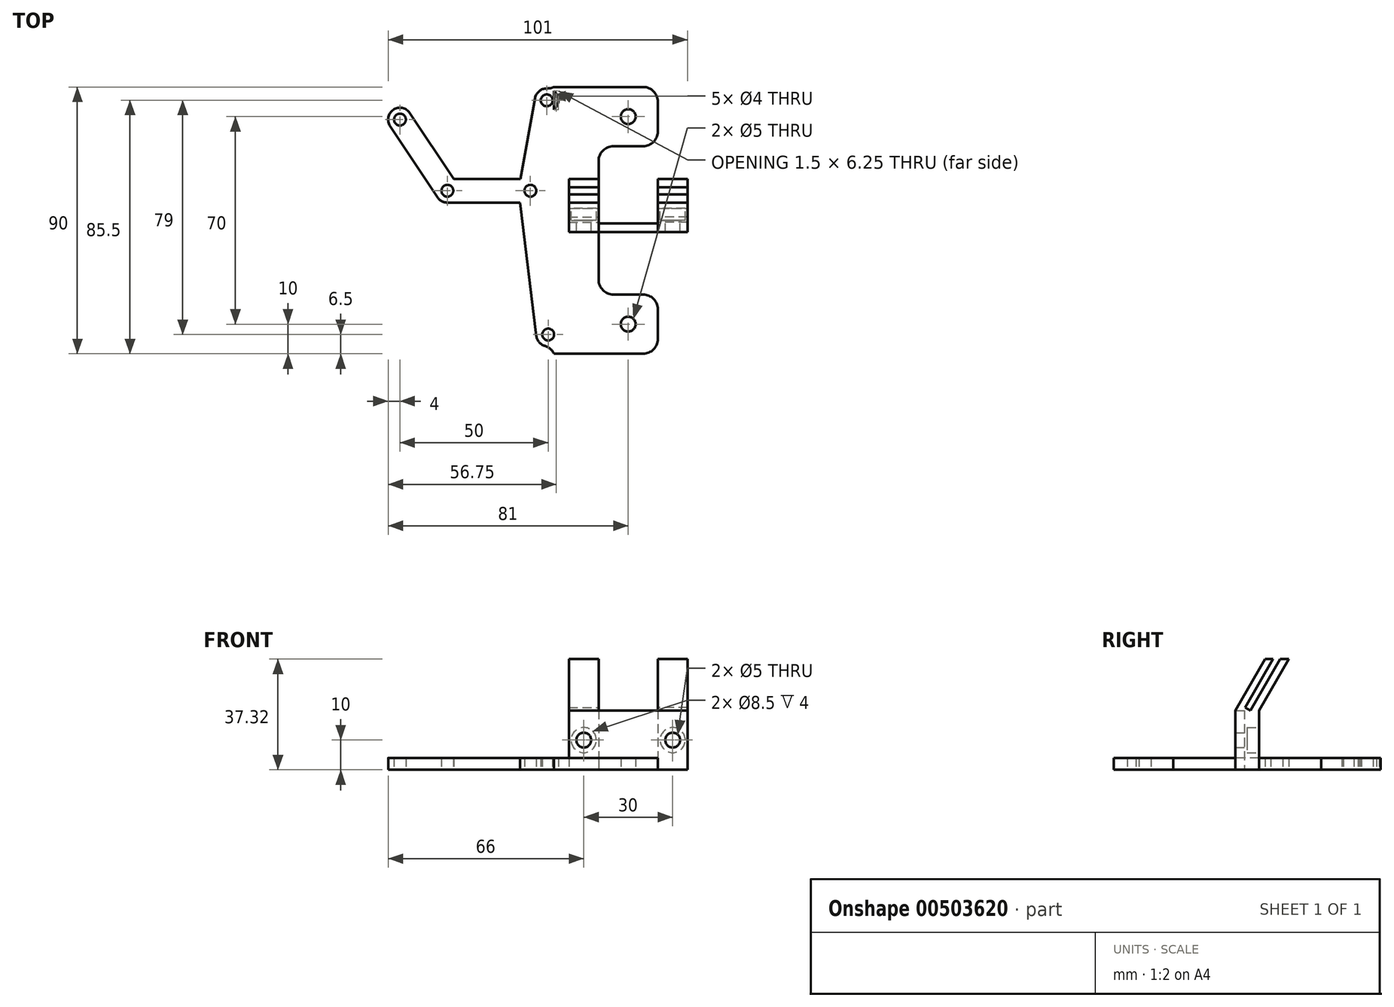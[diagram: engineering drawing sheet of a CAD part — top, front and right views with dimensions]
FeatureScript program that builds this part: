
annotation { "Feature Type Name" : "Feature", "Feature Type Description" : "" }
export const myFeature = defineFeature(function(context is Context, id is Id, definition is map)
    precondition{}
    {
        {
            var Q0;
            Q0=qCreatedBy(makeId("Top.planeOp"),FACE);
            var sketch = newSketch(context, id + "F0", { "sketchPlane" : qUnion([Q0])});
            skLineSegment(sketch, "E0.bottom", {"start": v(-20, 4) * mm, "end": v(20, 4) * mm});
            skLineSegment(sketch, "E0.top", {"start": v(-20, -4) * mm, "end": v(20, -4) * mm});
            skLineSegment(sketch, "E0.left", {"start": v(-20, 4) * mm, "end": v(-20, -4) * mm});
            skLineSegment(sketch, "E0.right", {"start": v(20, 4) * mm, "end": v(20, -4) * mm});
            skPoint(sketch, "E0.middle", {"position": v(0, 0) * mm});
            skLineSegment(sketch, "E1", {"start": v(-10, 4) * mm, "end": v(-10, -4) * mm});
            skLineSegment(sketch, "E2", {"start": v(10, 4) * mm, "end": v(10, -4) * mm});
            skLineSegment(sketch, "E3", {"start": v(-10, 0) * mm, "end": v(10, 0) * mm});
            skSolve(sketch);
        }
        {
            var Q0;
            {var subQ5=sQuery(id+"F0.wireOp",EDGE,"E3");Q0=makeQuery(id+"F0.imprint","IMPRINT",FACE,{"disambiguationData":[TD([[makeQuery(id+"F0.imprint","IMPRINT",EDGE,{"derivedFrom":subQ5}),-1.0]])]});}
            extrude(context, id + "F1", {"entities" : qUnion([Q0]), "depth" : 20 * mm, "offsetDistance" : 25 * mm});
        }
        {
            var Q0;
            {var subQ0=sQuery(id+"F0.wireOp",EDGE,"E0.left");Q0=makeQuery(id+"F0.imprint","IMPRINT",FACE,{"disambiguationData":[TD([[makeQuery(id+"F0.imprint","IMPRINT",EDGE,{"derivedFrom":subQ0}),1.0]])]});}
            var Q1;
            {var subQ4=sQuery(id+"F0.wireOp",EDGE,"E0.right");Q1=makeQuery(id+"F0.imprint","IMPRINT",FACE,{"disambiguationData":[TD([[makeQuery(id+"F0.imprint","IMPRINT",EDGE,{"derivedFrom":subQ4}),-1.0]])]});}
            extrude(context, id + "F2", {"entities" : qUnion([Q0, Q1]), "operationType" : NewBodyOperationType.ADD, "depth" : 20 * mm, "offsetDistance" : 25 * mm});
        }
        {
            var Q0;
            Q0=qCreatedBy(makeId("Right.planeOp"),FACE);
            var sketch = newSketch(context, id + "F3", { "sketchPlane" : qUnion([Q0])});
            skLineSegment(sketch, "E4.0", {"start": v(4, 20) * mm, "end": v(-4, 20) * mm});
            skLineSegment(sketch, "E5", {"start": v(-4, 20) * mm, "end": v(6, 37.32) * mm});
            skLineSegment(sketch, "E6", {"start": v(4, 20) * mm, "end": v(14, 37.32) * mm});
            skLineSegment(sketch, "E7", {"start": v(6, 37.32) * mm, "end": v(14, 37.32) * mm});
            skLineSegment(sketch, "E8", {"start": v(8.77, 37.32) * mm, "end": v(-1.23, 20) * mm});
            skLineSegment(sketch, "E9", {"start": v(11.14, 37.32) * mm, "end": v(1.14, 20) * mm});
            skLineSegment(sketch, "E10", {"start": v(1.14, 20) * mm, "end": v(-0.64, 21.02) * mm});
            skSolve(sketch);
        }
        {
            var Q0;
            {var subQ1=sQuery(id+"F3.wireOp",EDGE,"E5");Q0=makeQuery(id+"F3.imprint","IMPRINT",FACE,{"disambiguationData":[TD([[makeQuery(id+"F3.imprint","IMPRINT",EDGE,{"derivedFrom":subQ1}),-1.0]])]});}
            var Q1;
            {var subQ3=sQuery(id+"F3.wireOp",EDGE,"E10");Q1=makeQuery(id+"F3.imprint","IMPRINT",FACE,{"disambiguationData":[TD([[makeQuery(id+"F3.imprint","IMPRINT",EDGE,{"derivedFrom":subQ3}),1.0]])]});}
            var Q2;
            {var subQ0=sQuery(id+"F3.wireOp",EDGE,"E6");Q2=makeQuery(id+"F3.imprint","IMPRINT",FACE,{"disambiguationData":[TD([[makeQuery(id+"F3.imprint","IMPRINT",EDGE,{"derivedFrom":subQ0}),1.0]])]});}
            var Q3;
            Q3=makeQuery(id+"F2.opExtrude","SWEPT_FACE",FACE,{"disambiguationData":[OSD([sQuery(id+"F0.wireOp",EDGE,"E0.right")])]});
            var Q4;
            Q4=makeQuery(id+"F2.opExtrude","SWEPT_FACE",FACE,{"disambiguationData":[OSD([sQuery(id+"F0.wireOp",EDGE,"E2")])]});
            extrude(context, id + "F4", {"entities" : qUnion([Q0, Q1, Q2]), "operationType" : NewBodyOperationType.ADD, "endBound" : BoundingType.UP_TO_SURFACE, "depth" : 25 * mm, "endBoundEntityFace" : qUnion([Q3]), "offsetDistance" : 25 * mm, "hasSecondDirection" : true, "secondDirectionBound" : SecondDirectionBoundingType.UP_TO_SURFACE, "secondDirectionOppositeDirection" : false, "secondDirectionDepth" : 14.1 * mm, "secondDirectionBoundEntityFace" : qUnion([Q4])});
        }
        {
            var Q0;
            {var subQ0=sQuery(id+"F3.wireOp",EDGE,"E6");Q0=makeQuery(id+"F3.imprint","IMPRINT",FACE,{"disambiguationData":[TD([[makeQuery(id+"F3.imprint","IMPRINT",EDGE,{"derivedFrom":subQ0}),1.0]])]});}
            var Q1;
            {var subQ1=sQuery(id+"F3.wireOp",EDGE,"E5");Q1=makeQuery(id+"F3.imprint","IMPRINT",FACE,{"disambiguationData":[TD([[makeQuery(id+"F3.imprint","IMPRINT",EDGE,{"derivedFrom":subQ1}),-1.0]])]});}
            var Q2;
            {var subQ3=sQuery(id+"F3.wireOp",EDGE,"E10");Q2=makeQuery(id+"F3.imprint","IMPRINT",FACE,{"disambiguationData":[TD([[makeQuery(id+"F3.imprint","IMPRINT",EDGE,{"derivedFrom":subQ3}),1.0]])]});}
            var Q3;
            Q3=makeQuery(id+"F2.opExtrude","SWEPT_FACE",FACE,{"disambiguationData":[OSD([sQuery(id+"F0.wireOp",EDGE,"E0.left")])]});
            var Q4;
            Q4=makeQuery(id+"F2.opExtrude","SWEPT_FACE",FACE,{"disambiguationData":[OSD([sQuery(id+"F0.wireOp",EDGE,"E1")])]});
            extrude(context, id + "F5", {"entities" : qUnion([Q0, Q1, Q2]), "operationType" : NewBodyOperationType.ADD, "endBound" : BoundingType.UP_TO_SURFACE, "oppositeDirection" : true, "depth" : 25 * mm, "endBoundEntityFace" : qUnion([Q3]), "offsetDistance" : 25 * mm, "hasSecondDirection" : true, "secondDirectionBound" : SecondDirectionBoundingType.UP_TO_SURFACE, "secondDirectionOppositeDirection" : true, "secondDirectionDepth" : 25 * mm, "secondDirectionBoundEntityFace" : qUnion([Q4])});
        }
        {
            var Q0;
            {var subQ0=sQuery(id+"F0.wireOp",EDGE,"E0.bottom");Q0=makeQuery(id+"F2.opExtrude","SWEPT_FACE",FACE,{"disambiguationData":[OSD([subQ0]),TDD([makeQuery(id+"F0.imprint","IMPRINT",EDGE,{"disambiguationData":[TD([[makeQuery(id+"F0.imprint","INTERSECT",VERTEX,{"derivedFrom":[subQ0,sQuery(id+"F0.wireOp",EDGE,"E0.right")]}),1.0]])],"derivedFrom":subQ0})])]});}
            var sketch = newSketch(context, id + "F6", { "sketchPlane" : qUnion([Q0])});
            skLineSegment(sketch, "E11.0.0", {"start": v(10, 0) * mm, "end": v(20, 0) * mm});
            skLineSegment(sketch, "E11.0.1", {"start": v(20, 0) * mm, "end": v(20, 20) * mm});
            skLineSegment(sketch, "E11.0.2", {"start": v(20, 20) * mm, "end": v(10, 20) * mm});
            skLineSegment(sketch, "E11.0.3", {"start": v(10, 20) * mm, "end": v(10, 0) * mm});
            skCircle(sketch, "E12", {"center": v(-15, 10) * mm, "radius": 4.25 * mm});
            skPoint(sketch, "E12.centerSnap0", {"position": v(-15, 20) * mm});
            skPoint(sketch, "E12.centerSnap1", {"position": v(-20, 10) * mm});
            skCircle(sketch, "E13", {"center": v(15, 10) * mm, "radius": 4.25 * mm});
            skPoint(sketch, "E13.centerSnap0", {"position": v(10, 10) * mm});
            skPoint(sketch, "E13.centerSnap1", {"position": v(15, 20) * mm});
            skCircle(sketch, "E14", {"center": v(-15, 10) * mm, "radius": 2.5 * mm});
            skCircle(sketch, "E15", {"center": v(15, 10) * mm, "radius": 2.5 * mm});
            skSolve(sketch);
        }
        {
            var Q0;
            Q0=makeQuery(id+"F6.imprint","IMPRINT",FACE,{"disambiguationData":[TD([[makeQuery(id+"F6.imprint","IMPRINT",EDGE,{"derivedFrom":sQuery(id+"F6.wireOp",EDGE,"E14")}),1.0]])]});
            var Q1;
            Q1=makeQuery(id+"F6.imprint","IMPRINT",FACE,{"disambiguationData":[TD([[makeQuery(id+"F6.imprint","IMPRINT",EDGE,{"derivedFrom":sQuery(id+"F6.wireOp",EDGE,"E15")}),1.0]])]});
            extrude(context, id + "F7", {"entities" : qUnion([Q0, Q1]), "operationType" : NewBodyOperationType.REMOVE, "oppositeDirection" : true, "depth" : 25 * mm, "offsetDistance" : 25 * mm});
        }
        {
            var Q0;
            Q0=makeQuery(id+"F6.imprint","IMPRINT",FACE,{"disambiguationData":[TD([[makeQuery(id+"F6.imprint","IMPRINT",EDGE,{"derivedFrom":sQuery(id+"F6.wireOp",EDGE,"E12")}),1.0]])]});
            var Q1;
            Q1=makeQuery(id+"F6.imprint","IMPRINT",FACE,{"disambiguationData":[TD([[makeQuery(id+"F6.imprint","IMPRINT",EDGE,{"derivedFrom":sQuery(id+"F6.wireOp",EDGE,"E13")}),1.0]])]});
            extrude(context, id + "F8", {"entities" : qUnion([Q0, Q1]), "operationType" : NewBodyOperationType.REMOVE, "oppositeDirection" : true, "depth" : 4 * mm, "offsetDistance" : 25 * mm});
        }
        {
            var Q0;
            Q0=makeQuery(id+"F1.opExtrude","SWEPT_FACE",FACE,{"disambiguationData":[OSD([sQuery(id+"F0.wireOp",EDGE,"E3")])]});
            extrude(context, id + "F9", {"entities" : qUnion([Q0]), "operationType" : NewBodyOperationType.REMOVE, "oppositeDirection" : true, "depth" : 1 * mm, "offsetDistance" : 25 * mm});
        }
        {
            var Q0;
            Q0=qCreatedBy(makeId("Top.planeOp"),FACE);
            var sketch = newSketch(context, id + "F10", { "sketchPlane" : qUnion([Q0])});
            skLineSegment(sketch, "E16.bottom", {"start": v(-10, 45) * mm, "end": v(10, 45) * mm});
            skLineSegment(sketch, "E16.top", {"start": v(-10, -45) * mm, "end": v(10, -45) * mm});
            skLineSegment(sketch, "E16.left", {"start": v(-10, 45) * mm, "end": v(-10, -45) * mm});
            skLineSegment(sketch, "E16.right", {"start": v(10, 45) * mm, "end": v(10, -45) * mm});
            skPoint(sketch, "E16.middle", {"position": v(0, 0) * mm});
            skLineSegment(sketch, "E17.bottom", {"start": v(-10, 45) * mm, "end": v(-25, 45) * mm});
            skLineSegment(sketch, "E17.top", {"start": v(-10, -45) * mm, "end": v(-25, -45) * mm});
            skLineSegment(sketch, "E17.right", {"start": v(-25, 45) * mm, "end": v(-25, -45) * mm});
            skPoint(sketch, "E18", {"position": v(-27.5, 40.5) * mm});
            skCircle(sketch, "E19", {"center": v(-27.5, 40.5) * mm, "radius": 2 * mm});
            skPoint(sketch, "E20", {"position": v(-27, -38.5) * mm});
            skCircle(sketch, "E21", {"center": v(-27, -38.5) * mm, "radius": 2 * mm});
            skPoint(sketch, "E22", {"position": v(-33, 10) * mm});
            skPoint(sketch, "E23", {"position": v(-61, 10) * mm});
            skPoint(sketch, "E24", {"position": v(-77, 34) * mm});
            skCircle(sketch, "E25", {"center": v(-77, 34) * mm, "radius": 2 * mm});
            skCircle(sketch, "E26", {"center": v(-61, 10) * mm, "radius": 2 * mm});
            skCircle(sketch, "E27", {"center": v(-33, 10) * mm, "radius": 2 * mm});
            skCircle(sketch, "E28", {"center": v(-77, 34) * mm, "radius": 4 * mm});
            skCircle(sketch, "E29", {"center": v(-61, 10) * mm, "radius": 4 * mm});
            skCircle(sketch, "E30", {"center": v(-33, 10) * mm, "radius": 4 * mm});
            skCircle(sketch, "E31", {"center": v(-27.5, 40.5) * mm, "radius": 4 * mm});
            skCircle(sketch, "E32", {"center": v(-27, -38.5) * mm, "radius": 4 * mm});
            skLineSegment(sketch, "E33", {"start": v(-77, 34) * mm, "end": v(-61, 10) * mm, "construction": true});
            skLineSegment(sketch, "E34", {"start": v(-61, 10) * mm, "end": v(-33, 10) * mm, "construction": true});
            skLineSegment(sketch, "E35", {"start": v(-33, 10) * mm, "end": v(-27.5, 40.5) * mm, "construction": true});
            skLineSegment(sketch, "E36", {"start": v(-33, 10) * mm, "end": v(-27, -38.5) * mm, "construction": true});
            skLineSegment(sketch, "E37", {"start": v(-33, 14) * mm, "end": v(-25, 14) * mm});
            skLineSegment(sketch, "E38", {"start": v(-33, 6) * mm, "end": v(-25, 6) * mm});
            skLineSegment(sketch, "E39", {"start": v(-27.5, 44.5) * mm, "end": v(-25, 44.5) * mm});
            skLineSegment(sketch, "E40", {"start": v(-27.5, 36.5) * mm, "end": v(-25, 36.5) * mm});
            skLineSegment(sketch, "E41", {"start": v(-27, -34.5) * mm, "end": v(-25, -34.5) * mm});
            skLineSegment(sketch, "E42", {"start": v(-27, -42.5) * mm, "end": v(-25, -42.5) * mm});
            skLineSegment(sketch, "E43.0", {"start": v(-36.97, 9.5) * mm, "end": v(-30.97, -39) * mm});
            skLineSegment(sketch, "E44.0", {"start": v(-29.03, 10.5) * mm, "end": v(-23.03, -38) * mm});
            skLineSegment(sketch, "E45.0", {"start": v(-29.06, 9.3) * mm, "end": v(-23.56, 39.8) * mm});
            skLineSegment(sketch, "E46.0", {"start": v(-36.94, 10.7) * mm, "end": v(-31.44, 41.2) * mm});
            skLineSegment(sketch, "E47.0", {"start": v(-80.33, 31.78) * mm, "end": v(-64.33, 7.78) * mm});
            skLineSegment(sketch, "E48.0", {"start": v(-73.67, 36.22) * mm, "end": v(-57.67, 12.22) * mm});
            skLineSegment(sketch, "E49.0", {"start": v(-61, 6) * mm, "end": v(-33, 6) * mm});
            skLineSegment(sketch, "E50.0", {"start": v(-61, 14) * mm, "end": v(-33, 14) * mm});
            skCircle(sketch, "E51", {"center": v(0, 35) * mm, "radius": 2.5 * mm});
            skPoint(sketch, "E51.centerSnap0", {"position": v(0, 45) * mm});
            skCircle(sketch, "E52", {"center": v(0, -35) * mm, "radius": 2.5 * mm});
            skPoint(sketch, "E52.centerSnap0", {"position": v(0, -45) * mm});
            skLineSegment(sketch, "E53.bottom", {"start": v(-10, 25) * mm, "end": v(10, 25) * mm});
            skLineSegment(sketch, "E53.top", {"start": v(-10, -25) * mm, "end": v(10, -25) * mm});
            skLineSegment(sketch, "E53.left", {"start": v(-10, 25) * mm, "end": v(-10, -25) * mm});
            skLineSegment(sketch, "E53.right", {"start": v(10, 25) * mm, "end": v(10, -25) * mm});
            skSolve(sketch);
        }
        {
            var Q0;
            {var subQ1=sQuery(id+"F10.wireOp",EDGE,"E16.bottom");Q0=makeQuery(id+"F10.imprint","IMPRINT",FACE,{"disambiguationData":[TD([[makeQuery(id+"F10.imprint","IMPRINT",EDGE,{"derivedFrom":subQ1}),-1.0]])]});}
            var Q1;
            {var subQ12=sQuery(id+"F10.wireOp",EDGE,"E17.bottom");Q1=makeQuery(id+"F10.imprint","IMPRINT",FACE,{"disambiguationData":[TD([[makeQuery(id+"F10.imprint","IMPRINT",EDGE,{"derivedFrom":subQ12}),1.0]])]});}
            var Q2;
            {var subQ1=sQuery(id+"F10.wireOp",EDGE,"E16.top");Q2=makeQuery(id+"F10.imprint","IMPRINT",FACE,{"disambiguationData":[TD([[makeQuery(id+"F10.imprint","IMPRINT",EDGE,{"derivedFrom":subQ1}),1.0]])]});}
            var Q3;
            {var subQ7=sQuery(id+"F10.wireOp",EDGE,"E41");Q3=makeQuery(id+"F10.imprint","IMPRINT",FACE,{"disambiguationData":[TD([[makeQuery(id+"F10.imprint","IMPRINT",EDGE,{"derivedFrom":subQ7}),1.0]])]});}
            var Q4;
            {var subQ5=sQuery(id+"F10.wireOp",EDGE,"E37");var subQ6=sQuery(id+"F10.wireOp",EDGE,"E17.right");var subQ7=makeQuery(id+"F10.imprint","INTERSECT",VERTEX,{"derivedFrom":[subQ6,subQ5]});Q4=makeQuery(id+"F10.imprint","IMPRINT",FACE,{"disambiguationData":[TD([[makeQuery(id+"F10.imprint","IMPRINT",EDGE,{"disambiguationData":[TD([[subQ7,-1.0]])],"derivedFrom":subQ6}),-1.0]])]});}
            var Q5;
            {var subQ0=sQuery(id+"F10.wireOp",EDGE,"E17.right");var subQ1=makeQuery(id+"F10.imprint","INTERSECT",VERTEX,{"derivedFrom":[subQ0,sQuery(id+"F10.wireOp",EDGE,"E41")]});Q5=makeQuery(id+"F10.imprint","IMPRINT",FACE,{"disambiguationData":[TD([[makeQuery(id+"F10.imprint","IMPRINT",EDGE,{"disambiguationData":[TD([[subQ1,1.0]])],"derivedFrom":subQ0}),1.0]])]});}
            var Q6;
            {var subQ0=sQuery(id+"F10.wireOp",EDGE,"E41");Q6=makeQuery(id+"F10.imprint","IMPRINT",FACE,{"disambiguationData":[TD([[makeQuery(id+"F10.imprint","IMPRINT",EDGE,{"derivedFrom":subQ0}),-1.0]])]});}
            var Q7;
            {var subQ0=sQuery(id+"F10.wireOp",EDGE,"E17.right");var subQ1=makeQuery(id+"F10.imprint","INTERSECT",VERTEX,{"derivedFrom":[subQ0,sQuery(id+"F10.wireOp",EDGE,"E21")]});Q7=makeQuery(id+"F10.imprint","IMPRINT",FACE,{"disambiguationData":[TD([[makeQuery(id+"F10.imprint","IMPRINT",EDGE,{"disambiguationData":[TD([[subQ1,1.0]])],"derivedFrom":subQ0}),1.0]])]});}
            var Q8;
            {var subQ4=sQuery(id+"F10.wireOp",EDGE,"E21");Q8=makeQuery(id+"F10.imprint","IMPRINT",FACE,{"disambiguationData":[TD([[makeQuery(id+"F10.imprint","IMPRINT",EDGE,{"derivedFrom":subQ4}),-1.0]])]});}
            var Q9;
            {var subQ0=sQuery(id+"F10.wireOp",EDGE,"E42");Q9=makeQuery(id+"F10.imprint","IMPRINT",FACE,{"disambiguationData":[TD([[makeQuery(id+"F10.imprint","IMPRINT",EDGE,{"derivedFrom":subQ0}),1.0]])]});}
            var Q10;
            {var subQ0=sQuery(id+"F10.wireOp",EDGE,"E38");var subQ1=sQuery(id+"F10.wireOp",EDGE,"E17.right");var subQ2=makeQuery(id+"F10.imprint","INTERSECT",VERTEX,{"derivedFrom":[subQ1,subQ0]});Q10=makeQuery(id+"F10.imprint","IMPRINT",FACE,{"disambiguationData":[TD([[makeQuery(id+"F10.imprint","IMPRINT",EDGE,{"disambiguationData":[TD([[subQ2,-1.0]])],"derivedFrom":subQ1}),-1.0]])]});}
            var Q11;
            {var subQ0=sQuery(id+"F10.wireOp",EDGE,"E37");var subQ1=sQuery(id+"F10.wireOp",EDGE,"E17.right");var subQ2=makeQuery(id+"F10.imprint","INTERSECT",VERTEX,{"derivedFrom":[subQ1,subQ0]});Q11=makeQuery(id+"F10.imprint","IMPRINT",FACE,{"disambiguationData":[TD([[makeQuery(id+"F10.imprint","IMPRINT",EDGE,{"disambiguationData":[TD([[subQ2,1.0]])],"derivedFrom":subQ1}),-1.0]])]});}
            var Q12;
            {var subQ0=sQuery(id+"F10.wireOp",EDGE,"E38");var subQ5=sQuery(id+"F10.wireOp",EDGE,"E44.0");var subQ6=makeQuery(id+"F10.imprint","INTERSECT",VERTEX,{"derivedFrom":[subQ0,subQ5]});Q12=makeQuery(id+"F10.imprint","IMPRINT",FACE,{"disambiguationData":[TD([[makeQuery(id+"F10.imprint","IMPRINT",EDGE,{"disambiguationData":[TD([[subQ6,1.0]])],"derivedFrom":subQ5}),-1.0]])]});}
            var Q13;
            {var subQ1=sQuery(id+"F10.wireOp",EDGE,"E30");var subQ3=sQuery(id+"F10.wireOp",EDGE,"E43.0");var subQ4=makeQuery(id+"F10.imprint","INTERSECT",VERTEX,{"derivedFrom":[subQ1,subQ3]});Q13=makeQuery(id+"F10.imprint","IMPRINT",FACE,{"disambiguationData":[TD([[makeQuery(id+"F10.imprint","IMPRINT",EDGE,{"disambiguationData":[TD([[subQ4,-1.0]])],"derivedFrom":subQ3}),1.0]])]});}
            var Q14;
            {var subQ1=sQuery(id+"F10.wireOp",EDGE,"E30");var subQ3=sQuery(id+"F10.wireOp",EDGE,"E46.0");var subQ4=makeQuery(id+"F10.imprint","INTERSECT",VERTEX,{"derivedFrom":[subQ1,subQ3]});Q14=makeQuery(id+"F10.imprint","IMPRINT",FACE,{"disambiguationData":[TD([[makeQuery(id+"F10.imprint","IMPRINT",EDGE,{"disambiguationData":[TD([[subQ4,-1.0]])],"derivedFrom":subQ3}),-1.0]])]});}
            var Q15;
            {var subQ1=sQuery(id+"F10.wireOp",EDGE,"E30");var subQ3=sQuery(id+"F10.wireOp",EDGE,"E44.0");var subQ4=makeQuery(id+"F10.imprint","INTERSECT",VERTEX,{"derivedFrom":[subQ1,subQ3]});Q15=makeQuery(id+"F10.imprint","IMPRINT",FACE,{"disambiguationData":[TD([[makeQuery(id+"F10.imprint","IMPRINT",EDGE,{"disambiguationData":[TD([[subQ4,-1.0]])],"derivedFrom":subQ3}),1.0]])]});}
            var Q16;
            {var subQ0=sQuery(id+"F10.wireOp",EDGE,"E40");Q16=makeQuery(id+"F10.imprint","IMPRINT",FACE,{"disambiguationData":[TD([[makeQuery(id+"F10.imprint","IMPRINT",EDGE,{"derivedFrom":subQ0}),-1.0]])]});}
            var Q17;
            {var subQ0=sQuery(id+"F10.wireOp",EDGE,"E17.right");var subQ1=makeQuery(id+"F10.imprint","INTERSECT",VERTEX,{"derivedFrom":[subQ0,sQuery(id+"F10.wireOp",EDGE,"E40")]});Q17=makeQuery(id+"F10.imprint","IMPRINT",FACE,{"disambiguationData":[TD([[makeQuery(id+"F10.imprint","IMPRINT",EDGE,{"disambiguationData":[TD([[subQ1,1.0]])],"derivedFrom":subQ0}),1.0]])]});}
            var Q18;
            {var subQ0=sQuery(id+"F10.wireOp",EDGE,"E40");Q18=makeQuery(id+"F10.imprint","IMPRINT",FACE,{"disambiguationData":[TD([[makeQuery(id+"F10.imprint","IMPRINT",EDGE,{"derivedFrom":subQ0}),1.0]])]});}
            var Q19;
            Q19=makeQuery(id+"F10.imprint","IMPRINT",FACE,{"disambiguationData":[TD([[makeQuery(id+"F10.imprint","IMPRINT",EDGE,{"derivedFrom":sQuery(id+"F10.wireOp",EDGE,"E19")}),-1.0]])]});
            var Q20;
            {var subQ0=sQuery(id+"F10.wireOp",EDGE,"E31");var subQ1=sQuery(id+"F10.wireOp",EDGE,"E17.right");var subQ2=makeQuery(id+"F10.imprint","INTERSECT",VERTEX,{"disambiguationData":[OD(0.0)],"derivedFrom":[subQ1,subQ0]});Q20=makeQuery(id+"F10.imprint","IMPRINT",FACE,{"disambiguationData":[TD([[makeQuery(id+"F10.imprint","IMPRINT",EDGE,{"disambiguationData":[TD([[subQ2,-1.0]])],"derivedFrom":subQ1}),1.0]])]});}
            var Q21;
            {var subQ0=sQuery(id+"F10.wireOp",EDGE,"E39");Q21=makeQuery(id+"F10.imprint","IMPRINT",FACE,{"disambiguationData":[TD([[makeQuery(id+"F10.imprint","IMPRINT",EDGE,{"derivedFrom":subQ0}),-1.0]])]});}
            var Q22;
            {var subQ9=sQuery(id+"F10.wireOp",EDGE,"E48.0");var subQ10=sQuery(id+"F10.wireOp",EDGE,"E29");var subQ11=makeQuery(id+"F10.imprint","INTERSECT",VERTEX,{"derivedFrom":[subQ10,subQ9]});Q22=makeQuery(id+"F10.imprint","IMPRINT",FACE,{"disambiguationData":[TD([[makeQuery(id+"F10.imprint","IMPRINT",EDGE,{"disambiguationData":[TD([[subQ11,1.0]])],"derivedFrom":subQ10}),-1.0]])]});}
            var Q23;
            Q23=makeQuery(id+"F10.imprint","IMPRINT",FACE,{"disambiguationData":[TD([[makeQuery(id+"F10.imprint","IMPRINT",EDGE,{"derivedFrom":sQuery(id+"F10.wireOp",EDGE,"E26")}),-1.0]])]});
            var Q24;
            {var subQ0=sQuery(id+"F10.wireOp",EDGE,"E48.0");var subQ1=sQuery(id+"F10.wireOp",EDGE,"E29");var subQ2=makeQuery(id+"F10.imprint","INTERSECT",VERTEX,{"derivedFrom":[subQ1,subQ0]});Q24=makeQuery(id+"F10.imprint","IMPRINT",FACE,{"disambiguationData":[TD([[makeQuery(id+"F10.imprint","IMPRINT",EDGE,{"disambiguationData":[TD([[subQ2,-1.0]])],"derivedFrom":subQ1}),-1.0]])]});}
            var Q25;
            {var subQ5=sQuery(id+"F10.wireOp",EDGE,"E47.0");Q25=makeQuery(id+"F10.imprint","IMPRINT",FACE,{"disambiguationData":[TD([[makeQuery(id+"F10.imprint","IMPRINT",EDGE,{"derivedFrom":subQ5}),1.0]])]});}
            var Q26;
            Q26=makeQuery(id+"F10.imprint","IMPRINT",FACE,{"disambiguationData":[TD([[makeQuery(id+"F10.imprint","IMPRINT",EDGE,{"derivedFrom":sQuery(id+"F10.wireOp",EDGE,"E25")}),-1.0]])]});
            var Q27;
            Q27=makeQuery(id+"F10.imprint","IMPRINT",FACE,{"disambiguationData":[TD([[makeQuery(id+"F10.imprint","IMPRINT",EDGE,{"derivedFrom":sQuery(id+"F10.wireOp",EDGE,"E27")}),-1.0]])]});
            var Q28;
            {var subQ0=sQuery(id+"F10.wireOp",EDGE,"E44.0");var subQ1=sQuery(id+"F10.wireOp",EDGE,"E30");var subQ2=makeQuery(id+"F10.imprint","INTERSECT",VERTEX,{"derivedFrom":[subQ1,subQ0]});Q28=makeQuery(id+"F10.imprint","IMPRINT",FACE,{"disambiguationData":[TD([[makeQuery(id+"F10.imprint","IMPRINT",EDGE,{"disambiguationData":[TD([[subQ2,1.0]])],"derivedFrom":subQ1}),-1.0]])]});}
            extrude(context, id + "F11", {"entities" : qUnion([Q0, Q1, Q2, Q3, Q4, Q5, Q6, Q7, Q8, Q9, Q10, Q11, Q12, Q13, Q14, Q15, Q16, Q17, Q18, Q19, Q20, Q21, Q22, Q23, Q24, Q25, Q26, Q27, Q28]), "depth" : 4 * mm, "offsetDistance" : 25 * mm});
        }
        {
            var Q0;
            Q0=makeQuery(id+"F11.opExtrude","SWEPT_EDGE",EDGE,{"disambiguationData":[OSD([sQuery(id+"F10.wireOp",EDGE,"E17.right"),sQuery(id+"F10.wireOp",EDGE,"E42")])]});
            var Q1;
            Q1=makeQuery(id+"F11.opExtrude","SWEPT_EDGE",EDGE,{"disambiguationData":[OSD([sQuery(id+"F10.wireOp",EDGE,"E17.right"),sQuery(id+"F10.wireOp",EDGE,"E39")])]});
            fillet(context, id + "F12", {"entities" : qUnion([Q0, Q1]), "radius" : 5 * mm, "tangentPropagation" : true, "allowEdgeOverflow" : false});
        }
        {
            var Q0;
            Q0=makeQuery(id+"F11.opExtrude","SWEPT_EDGE",EDGE,{"disambiguationData":[OSD([sQuery(id+"F10.wireOp",EDGE,"E16.bottom"),sQuery(id+"F10.wireOp",EDGE,"E16.right")])]});
            var Q1;
            Q1=makeQuery(id+"F11.opExtrude","SWEPT_EDGE",EDGE,{"disambiguationData":[OSD([sQuery(id+"F10.wireOp",EDGE,"E16.right"),sQuery(id+"F10.wireOp",EDGE,"E53.bottom"),sQuery(id+"F10.wireOp",EDGE,"E53.right")])]});
            var Q2;
            Q2=makeQuery(id+"F11.opExtrude","SWEPT_EDGE",EDGE,{"disambiguationData":[OSD([sQuery(id+"F10.wireOp",EDGE,"E16.left"),sQuery(id+"F10.wireOp",EDGE,"E53.bottom"),sQuery(id+"F10.wireOp",EDGE,"E53.left")])]});
            var Q3;
            Q3=makeQuery(id+"F11.opExtrude","SWEPT_EDGE",EDGE,{"disambiguationData":[OSD([sQuery(id+"F10.wireOp",EDGE,"E16.left"),sQuery(id+"F10.wireOp",EDGE,"E53.top"),sQuery(id+"F10.wireOp",EDGE,"E53.left")])]});
            var Q4;
            Q4=makeQuery(id+"F11.opExtrude","SWEPT_EDGE",EDGE,{"disambiguationData":[OSD([sQuery(id+"F10.wireOp",EDGE,"E16.right"),sQuery(id+"F10.wireOp",EDGE,"E53.top"),sQuery(id+"F10.wireOp",EDGE,"E53.right")])]});
            var Q5;
            Q5=makeQuery(id+"F11.opExtrude","SWEPT_EDGE",EDGE,{"disambiguationData":[OSD([sQuery(id+"F10.wireOp",EDGE,"E16.top"),sQuery(id+"F10.wireOp",EDGE,"E16.right")])]});
            fillet(context, id + "F13", {"entities" : qUnion([Q0, Q1, Q2, Q3, Q4, Q5]), "radius" : 5 * mm, "tangentPropagation" : true, "allowEdgeOverflow" : false});
        }
    });
